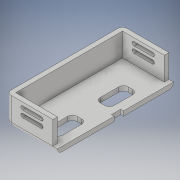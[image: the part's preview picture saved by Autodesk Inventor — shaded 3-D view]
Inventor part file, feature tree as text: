
AUTODESK INVENTOR PART (.ipt)
format: ipt  version: 2019.4 (Build 234330000, 330)  size: 200,192 bytes
history: native  units: mm
features: extrude x5, sketch x5, fillet x2, pattern_linear x1
ambient origin geometry x8: Origin, YZ Plane, XZ Plane, XY Plane, X Axis, Y Axis, Z Axis, Center Point
bodies: Solid1 (feature_tree)
feature tree (13):
  extrude  "Extrusion1"  Depth=115.0mm
  extrude  "Extrusion2"  Depth=5.0mm TaperAngle=0.0deg
  extrude  "Extrusion3"  Depth=115.0mm
  extrude  "Extrusion4"  Depth=25.0mm TaperAngle=0.0deg
  fillet  "Fillet1"  Radius=5.5mm
  fillet  "Fillet2"  Radius=10.0mm
  pattern_linear  "Rectangular Pattern1"  Spacing1=4.0mm  [1 undecoded]
  extrude  "Extrusion5"  Depth=125.0mm TaperAngle=0.0deg
  sketch  "Sketch1"  dims[d0=45.0mm d1=115.0mm]
  sketch  "Sketch2"  dims[d2=5.0mm d3=5.0mm d4=0.0mm]
  sketch  "Sketch3"  dims[d5=45.0mm d6=115.0mm]
  sketch  "Sketch4"  dims[d7=5.0mm d8=25.0mm d9=0.0mm d10=5.5mm d11=10.0mm]
  sketch  "Sketch5"  dims[d12=0.0mm d13=4.0mm d14=125.0mm d15=0.0mm d16=25.0mm d17=6.0mm d18=15.0mm d19=30.0mm d20=20.0mm d22=55.0mm d23=10.0mm d25=10.0mm d27=5.0mm d28=0.0mm d29=5.0mm d30=5.0mm d31=20.0mm d33=7.0mm d34=5.0mm d35=5.0mm d36=3.0mm d37=0.0mm]
note: 1 required parameter value undecoded (feature->parameter linkage not recoverable at this tier; creation-order binding heuristic only, values carry confidence <= 0.55)
